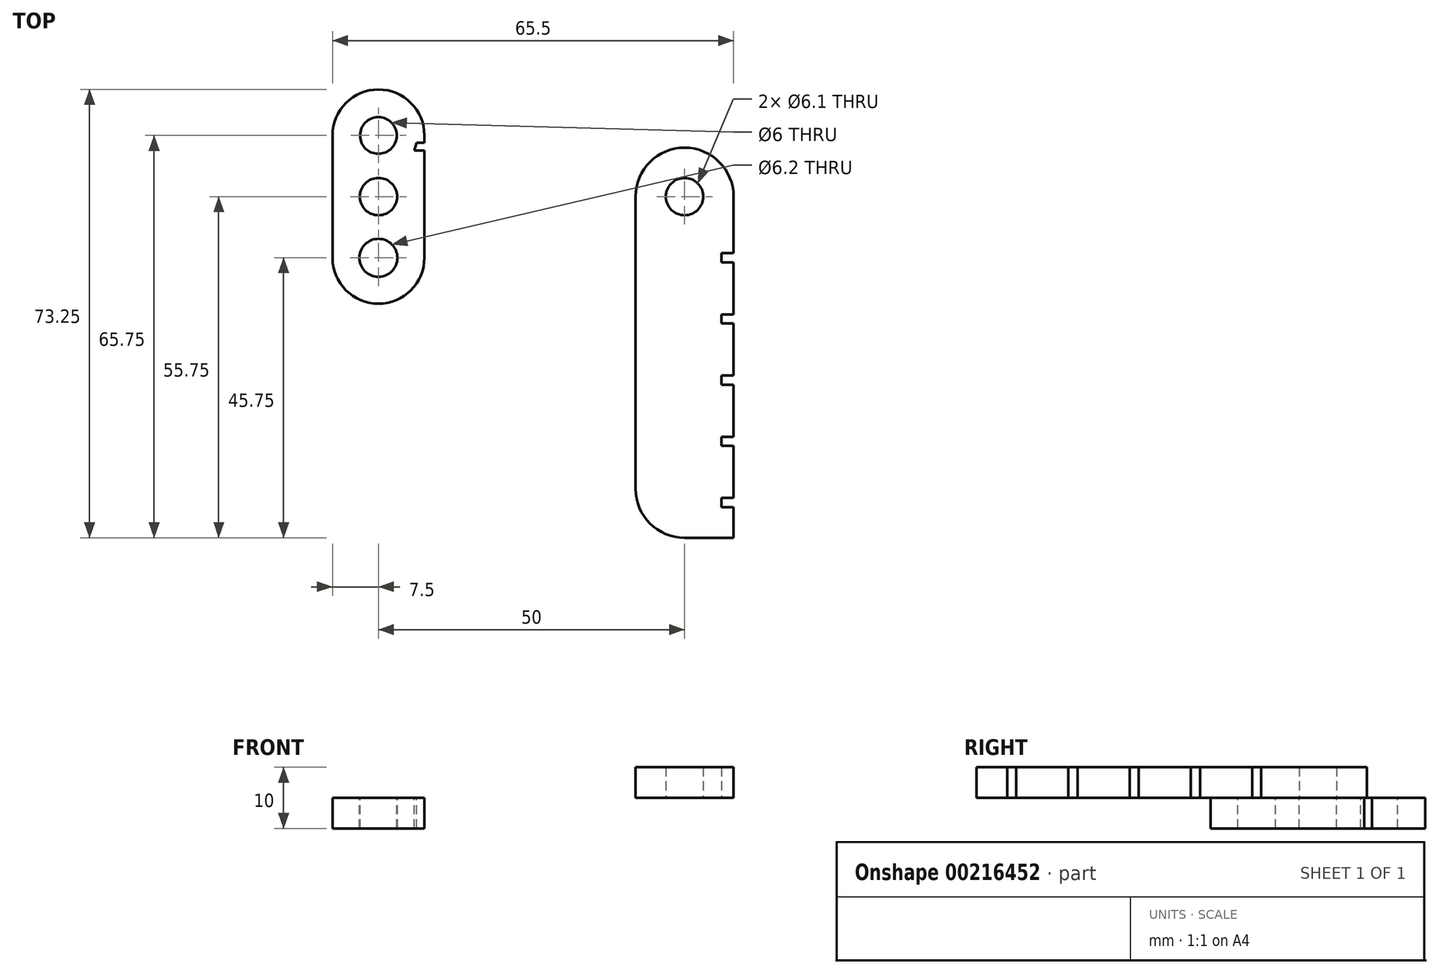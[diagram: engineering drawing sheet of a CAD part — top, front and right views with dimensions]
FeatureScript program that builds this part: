
annotation { "Feature Type Name" : "Feature", "Feature Type Description" : "" }
export const myFeature = defineFeature(function(context is Context, id is Id, definition is map)
    precondition{}
    {
        {
            var Q0;
            Q0=qCreatedBy(makeId("Top.planeOp"),FACE);
            var sketch = newSketch(context, id + "F0", { "sketchPlane" : qUnion([Q0])});
            skArc(sketch, "E0", {"start": v(7.5, 10) * mm, "mid": v(0, 17.5) * mm, "end": v(-7.5, 10) * mm});
            skArc(sketch, "E1.MirrorCS", {"start": v(7.5, -10) * mm, "mid": v(0, -17.5) * mm, "end": v(-7.5, -10) * mm});
            skLineSegment(sketch, "E2", {"start": v(7.5, 10) * mm, "end": v(7.5, 8.81) * mm});
            skLineSegment(sketch, "E3", {"start": v(-7.5, -10) * mm, "end": v(-7.5, 10) * mm});
            skLineSegment(sketch, "E4", {"start": v(7.5, 7.56) * mm, "end": v(5.86, 7.56) * mm});
            skLineSegment(sketch, "E5", {"start": v(5.86, 7.56) * mm, "end": v(6.24, 8.81) * mm});
            skLineSegment(sketch, "E6", {"start": v(6.24, 8.81) * mm, "end": v(7.5, 8.81) * mm});
            skLineSegment(sketch, "E7.trimOffspring", {"start": v(7.5, 7.56) * mm, "end": v(7.5, -10) * mm});
            skSolve(sketch);
        }
        {
            var Q0;
            Q0 = qSketchRegion(id + "F0", true);
            extrude(context, id + "F1", {"entities" : qUnion([Q0]), "oppositeDirection" : true, "depth" : 5 * mm});
        }
        {
            var Q0;
            Q0=makeQuery(id+"F1.opExtrude","CAP_FACE",FACE,{"disambiguationData":[OSD([sQuery(id+"F0.wireOp",EDGE,"E0"),sQuery(id+"F0.wireOp",EDGE,"E1.MirrorCS"),sQuery(id+"F0.wireOp",EDGE,"E2"),sQuery(id+"F0.wireOp",EDGE,"E3")])],"isStart":true});
            var sketch = newSketch(context, id + "F2", { "sketchPlane" : qUnion([Q0])});
            skCircle(sketch, "E8", {"center": v(0, 0) * mm, "radius": 3.05 * mm});
            skCircle(sketch, "E9", {"center": v(0, 10) * mm, "radius": 3 * mm});
            skCircle(sketch, "E10", {"center": v(0, -10) * mm, "radius": 3.1 * mm});
            skSolve(sketch);
        }
        {
            var Q0;
            Q0 = qSketchRegion(id + "F2", true);
            extrude(context, id + "F3", {"entities" : qUnion([Q0]), "operationType" : NewBodyOperationType.REMOVE, "oppositeDirection" : true, "depth" : 25 * mm});
        }
        {
            var Q0;
            Q0=qCreatedBy(makeId("Top.planeOp"),FACE);
            var sketch = newSketch(context, id + "F4", { "sketchPlane" : qUnion([Q0])});
            skCircle(sketch, "E11", {"center": v(50, 0) * mm, "radius": 3.05 * mm});
            skArc(sketch, "E12", {"start": v(58, 0) * mm, "mid": v(50, 8) * mm, "end": v(42, 0) * mm});
            skLineSegment(sketch, "E13", {"start": v(42, 0) * mm, "end": v(42, -47.75) * mm});
            skLineSegment(sketch, "E14", {"start": v(50, -55.75) * mm, "end": v(58, -55.75) * mm});
            skLineSegment(sketch, "E15", {"start": v(58, -55.75) * mm, "end": v(58, -50.75) * mm});
            skLineSegment(sketch, "E16", {"start": v(58, -10.75) * mm, "end": v(56, -10.75) * mm});
            skLineSegment(sketch, "E17", {"start": v(56, -9.25) * mm, "end": v(56, -10.75) * mm});
            skLineSegment(sketch, "E18", {"start": v(56, -9.25) * mm, "end": v(58, -9.25) * mm});
            skPoint(sketch, "E19", {"position": v(56, -10) * mm});
            skLineSegment(sketch, "E20.1.0.0", {"start": v(56, -19.25) * mm, "end": v(58, -19.25) * mm});
            skLineSegment(sketch, "E20.1.0.1", {"start": v(56, -19.25) * mm, "end": v(56, -20.75) * mm});
            skLineSegment(sketch, "E20.1.0.2", {"start": v(58, -20.75) * mm, "end": v(56, -20.75) * mm});
            skLineSegment(sketch, "E20.2.0.0", {"start": v(56, -29.25) * mm, "end": v(58, -29.25) * mm});
            skLineSegment(sketch, "E20.2.0.1", {"start": v(56, -29.25) * mm, "end": v(56, -30.75) * mm});
            skLineSegment(sketch, "E20.2.0.2", {"start": v(58, -30.75) * mm, "end": v(56, -30.75) * mm});
            skLineSegment(sketch, "E20.direction1", {"start": v(56, -9.25) * mm, "end": v(56, -19.25) * mm, "construction": true});
            skLineSegment(sketch, "E21.0.3.0", {"start": v(56, -39.25) * mm, "end": v(58, -39.25) * mm});
            skLineSegment(sketch, "E21.3.3.0", {"start": v(56, -39.25) * mm, "end": v(56, -40.75) * mm});
            skLineSegment(sketch, "E21.6.3.0", {"start": v(58, -40.75) * mm, "end": v(56, -40.75) * mm});
            skLineSegment(sketch, "E21.0.4.0", {"start": v(56, -49.25) * mm, "end": v(58, -49.25) * mm});
            skLineSegment(sketch, "E21.3.4.0", {"start": v(56, -49.25) * mm, "end": v(56, -50.75) * mm});
            skLineSegment(sketch, "E21.6.4.0", {"start": v(58, -50.75) * mm, "end": v(56, -50.75) * mm});
            skPoint(sketch, "E22.visualSharp", {"position": v(42, -55.75) * mm});
            skArc(sketch, "E22.filletArc", {"start": v(42, -47.75) * mm, "mid": v(44.34, -53.4) * mm, "end": v(50, -55.75) * mm});
            skLineSegment(sketch, "E23.trimOffspring", {"start": v(58, -9.25) * mm, "end": v(58, 0) * mm});
            skLineSegment(sketch, "E24.trimOffspring", {"start": v(58, -19.25) * mm, "end": v(58, -10.75) * mm});
            skLineSegment(sketch, "E25.trimOffspring", {"start": v(58, -29.25) * mm, "end": v(58, -20.75) * mm});
            skLineSegment(sketch, "E26.trimOffspring", {"start": v(58, -39.25) * mm, "end": v(58, -30.75) * mm});
            skLineSegment(sketch, "E27.trimOffspring", {"start": v(58, -49.25) * mm, "end": v(58, -40.75) * mm});
            skSolve(sketch);
        }
        {
            var Q0;
            Q0 = qSketchRegion(id + "F4", true);
            extrude(context, id + "F5", {"entities" : qUnion([Q0]), "depth" : 5 * mm});
        }
    });
